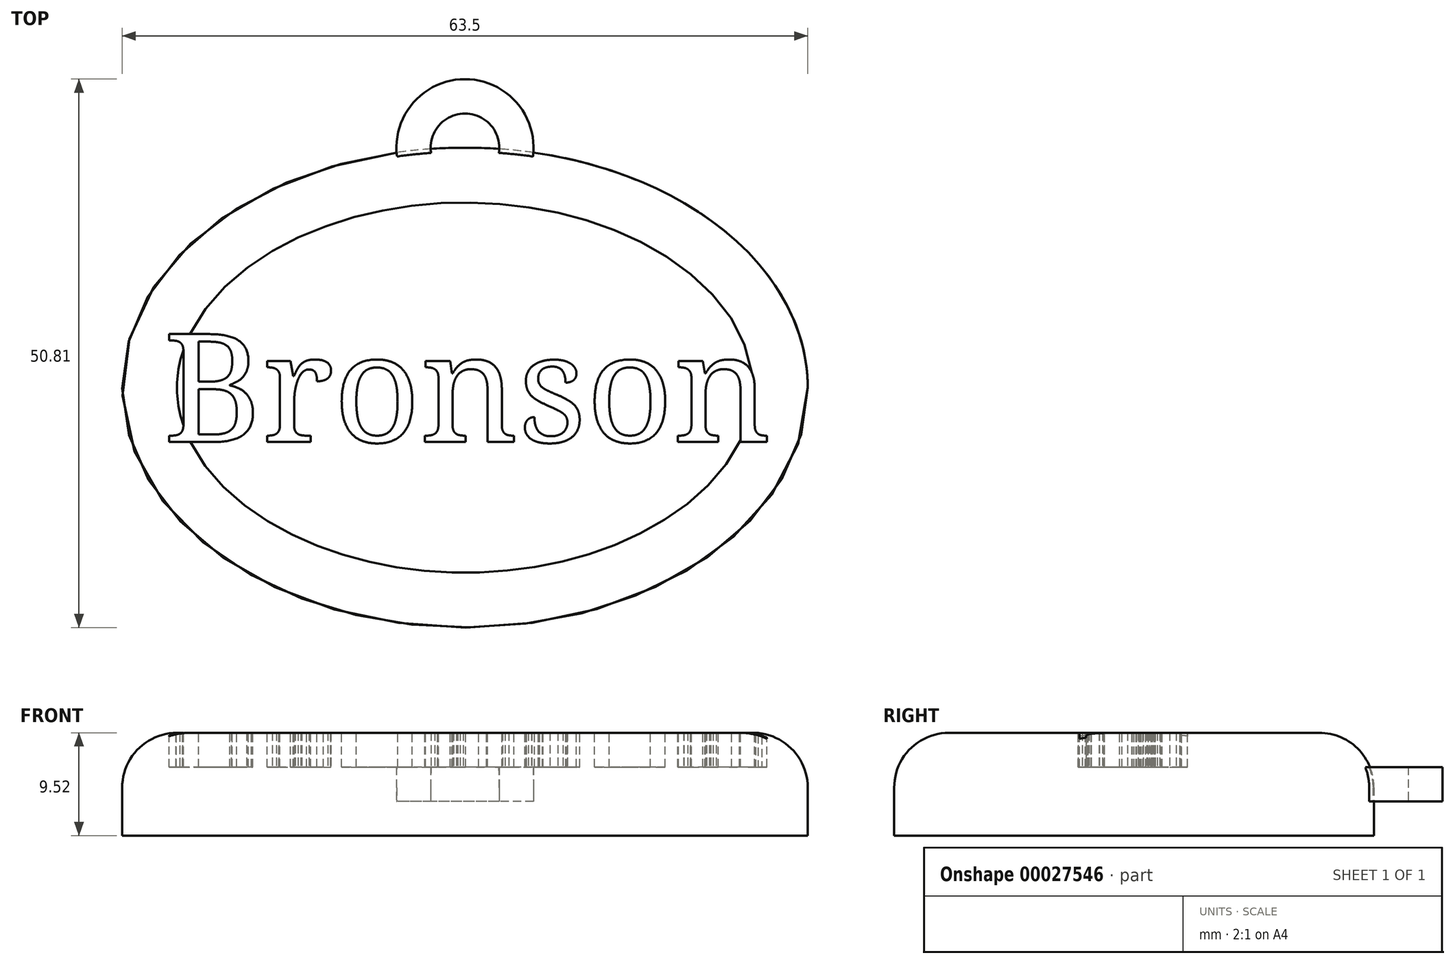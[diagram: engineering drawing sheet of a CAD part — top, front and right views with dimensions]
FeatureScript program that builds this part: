
annotation { "Feature Type Name" : "Feature", "Feature Type Description" : "" }
export const myFeature = defineFeature(function(context is Context, id is Id, definition is map)
    precondition{}
    {
        {
            var Q0;
            Q0=qCreatedBy(makeId("Top.planeOp"),FACE);
            var sketch = newSketch(context, id + "F0", { "sketchPlane" : qUnion([Q0])});
            skEllipse(sketch, "E0", {"center": v(0, 0) * mm, "majorRadius": 31.75 * mm, "minorRadius": 22.23 * mm, "majorAxis": v(1, 0)});
            skSolve(sketch);
        }
        {
            var Q0;
            Q0=makeQuery(id+"F0.imprint","IMPRINT",FACE,{"disambiguationData":[TD([[makeQuery(id+"F0.imprint","IMPRINT",EDGE,{"derivedFrom":sQuery(id+"F0.wireOp",EDGE,"E0")}),1.0]])]});
            extrude(context, id + "F1", {"entities" : qUnion([Q0]), "endBound" : BoundingType.SYMMETRIC, "depth" : 9.52 * mm});
        }
        {
            var Q0;
            Q0=qCreatedBy(makeId("Top.planeOp"),FACE);
            var sketch = newSketch(context, id + "F2", { "sketchPlane" : qUnion([Q0])});
            skCircle(sketch, "E1", {"center": v(0, 22.23) * mm, "radius": 6.35 * mm});
            skCircle(sketch, "E2", {"center": v(0, 22.23) * mm, "radius": 3.18 * mm});
            skEllipse(sketch, "E3.0", {"center": v(0, 0) * mm, "majorRadius": 31.75 * mm, "minorRadius": 22.23 * mm, "majorAxis": v(1, 0)});
            skSolve(sketch);
        }
        {
            var Q0;
            {var subQ0=sQuery(id+"F2.wireOp",EDGE,"E3.0");var subQ3=sQuery(id+"F2.wireOp",EDGE,"E1");var subQ4=makeQuery(id+"F2.imprint","INTERSECT",VERTEX,{"disambiguationData":[OD(0.0)],"derivedFrom":[subQ3,subQ0]});Q0=makeQuery(id+"F2.imprint","IMPRINT",FACE,{"disambiguationData":[TD([[makeQuery(id+"F2.imprint","IMPRINT",EDGE,{"disambiguationData":[TD([[subQ4,-1.0]])],"derivedFrom":subQ3}),1.0]])]});}
            extrude(context, id + "F3", {"entities" : qUnion([Q0]), "operationType" : NewBodyOperationType.ADD, "endBound" : BoundingType.SYMMETRIC, "depth" : 3.17 * mm});
        }
        {
            var Q0;
            Q0=makeQuery(id+"F1.opExtrude","CAP_FACE",FACE,{"disambiguationData":[OSD([sQuery(id+"F0.wireOp",EDGE,"E0")])],"isStart":false});
            var sketch = newSketch(context, id + "F4", { "sketchPlane" : qUnion([Q0])});
            skText(sketch, "E4", { "text": "Bronson", "fontName": "NotoSerif-Regular.ttf"});
            const initialGuessF4  = {"E4": [-0.02794, -0.00504, 1, 0, 0.01008]};
            skSetInitialGuess(sketch, initialGuessF4);
            skSolve(sketch);
        }
        {
            var Q0;
            Q0 = qSketchRegion(id + "F4", true);
            extrude(context, id + "F5", {"entities" : qUnion([Q0]), "operationType" : NewBodyOperationType.REMOVE, "oppositeDirection" : true, "depth" : 3.17 * mm});
        }
        {
            var Q0;
            Q0=makeQuery(id+"F1.opExtrude","CAP_EDGE",EDGE,{"disambiguationData":[OSD([sQuery(id+"F0.wireOp",EDGE,"E0")])],"isStart":false});
            fillet(context, id + "F6", {"entities" : qUnion([Q0]), "radius" : 5.08 * mm, "tangentPropagation" : true, "allowEdgeOverflow" : false});
        }
    });
